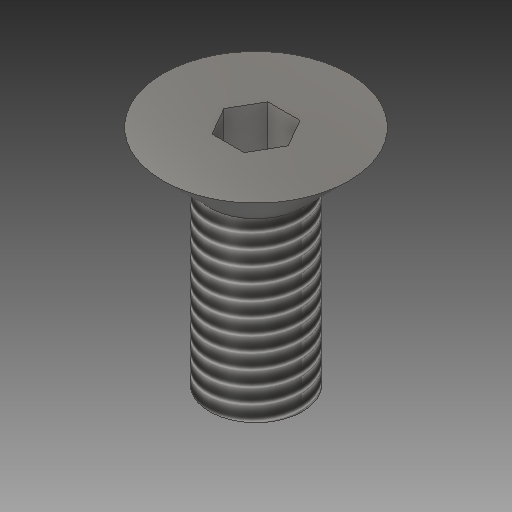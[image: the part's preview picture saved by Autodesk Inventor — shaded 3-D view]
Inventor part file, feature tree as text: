
AUTODESK INVENTOR PART (.ipt)
format: ipt  version: 2019 (Build 230136000, 136)  size: 158,720 bytes
history: native  units: mm
features: other x4, extrude x1
ambient origin geometry x8: Origin, YZ Plane, XZ Plane, XY Plane, X Axis, Y Axis, Z Axis, Center Point
bodies: Solid1 (feature_tree), Body (feature_tree)
feature tree (5):
  other  "Head"
  extrude  "Key Socket Cutout"  TaperAngle=0.0deg  [1 undecoded]
  other  "Head Revolution Profile"
  other  "Body Cross Section"
  other  "Key Socket Cutout Outline"
note: 1 required parameter value undecoded (feature->parameter linkage not recoverable at this tier; creation-order binding heuristic only, values carry confidence <= 0.55)
